# Revit family: Drain_Slotted_Hi-Cap_Zurn-Z888-18
name_source: partatom
category: Plumbing Fixtures
units: mm (PartAtom-declared; Revit-internal decimal feet)

## family parameters
Always vertical = Yes
Cut with Voids When Loaded = No
Maintain Annotation Orientation = No
OmniClass Number = 23.70.50.21.24.14
OmniClass Title = Deck Waste Water Drains
Part Type = Normal
Room Calculation Point = No
Round Connector Dimension = Use Radius
Shared = No
Work Plane-Based = No

## types (4) — shared parameters
Assembly Code = D2030300
CW Connection = No
Default Elevation = 10 "
Description = HI-CAP SLOTTED DRAINAGE SYSTEM FOR 18 [457] CORRUGATED PIPE OR EQUIVALENT
HW Connection = No
Main Material = Polymer - Zurn - LDPE - Black
Manufacturer = Zurn Water, LLC
Manufacurer Brand = Zurn
Model = Z888-18
Modified Date = 02/20/2026
Product Documentation Link = https://files.zurn.com
Product Installation Sheet URL = https://files.zurn.com
Product Page URL = https://www.zurn.com
Product data url = https://www.bimobject.com
URL = www.zurn.com
Vent Connection = No
WFU = 1
Waste Connection = Yes
zero-valued in all types: CWFU, HWFU

## per-type parameters (varying)
| type | End Outlet R for 18' & 24" | End Plate - 18"& 24" Outlet | End Plate - 8" & 12" Outlet | Nominal Diameter | Outlet Height | Pipe Size 'A' (Inner Diameter) | Pipe Size 'A' (Inner Radius) | Pipe Size 'A' (Nominal Radius) | Pipe Size 'A' (Outer Diameter) | Pipe Size 'A' (Outer Radius) |
| Z888-18 with 8 Inch No-Hub End Outlet | 18 " | No | Yes | 8 " | 17.75 " | 7.981 " | 3.991 " | 4 " | 8.625 " | 4.313 " |
| Z888-18 with 12 Inch No-Hub End Outlet | 18 " | No | Yes | 12 " | 15.25 " | 12 " | 6 " | 6 " | 12.75 " | 6.375 " |
| Z888-18 with 18 Inch No-Hub End Outlet | 18 " | Yes | No | 18 " | 15.75 " | 16.88 " | 8.44 " | 9 " | 18 " | 9 " |
| Z888-18 with 24 Inch No-Hub End Outlet(Custom Built) | 24 " | Yes | No | 24 " | 18.75 " | 22.63 " | 11.315 " | 12 " | 24 " | 12 " |

## geometry (parser evidence)
native form markers: Blend x4, Sweep x2
no freeform markers — native parametric forms only
